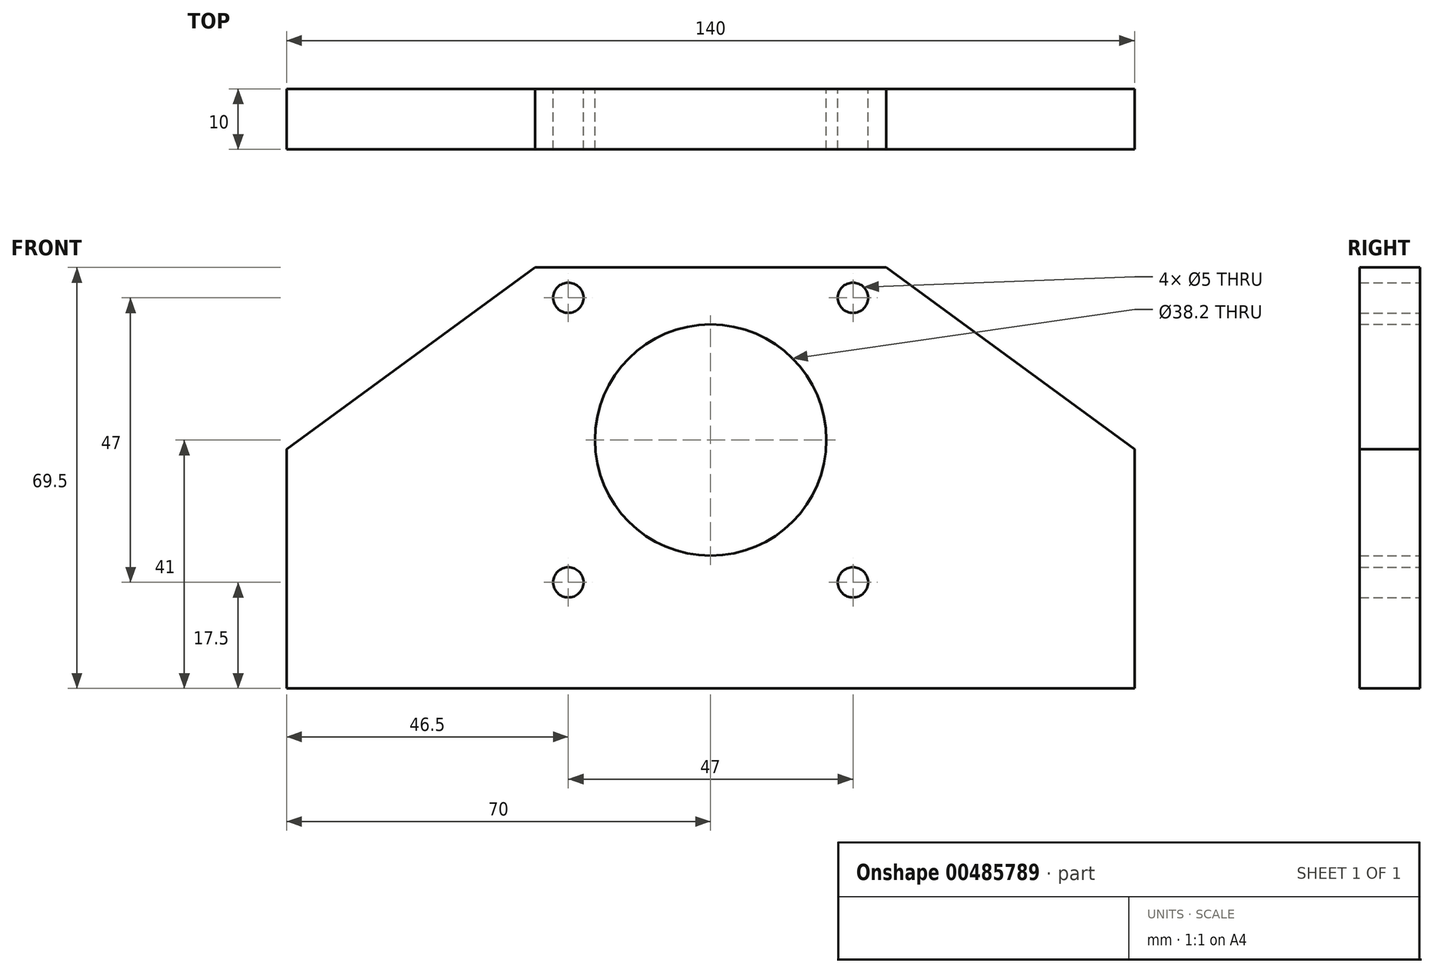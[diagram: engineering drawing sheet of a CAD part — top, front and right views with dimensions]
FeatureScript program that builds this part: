
annotation { "Feature Type Name" : "Feature", "Feature Type Description" : "" }
export const myFeature = defineFeature(function(context is Context, id is Id, definition is map)
    precondition{}
    {
        {
            var Q0;
            Q0=qCreatedBy(makeId("Front.planeOp"),FACE);
            var sketch = newSketch(context, id + "F0", { "sketchPlane" : qUnion([Q0])});
            skLineSegment(sketch, "E0.bottom", {"start": v(-23.5, 23.5) * mm, "end": v(23.5, 23.5) * mm, "construction": true});
            skLineSegment(sketch, "E0.top", {"start": v(-23.5, -23.5) * mm, "end": v(23.5, -23.5) * mm, "construction": true});
            skLineSegment(sketch, "E0.left", {"start": v(-23.5, 23.5) * mm, "end": v(-23.5, -23.5) * mm, "construction": true});
            skLineSegment(sketch, "E0.right", {"start": v(23.5, 23.5) * mm, "end": v(23.5, -23.5) * mm, "construction": true});
            skPoint(sketch, "E0.middle", {"position": v(0, 0) * mm});
            skLineSegment(sketch, "E1.bottom", {"start": v(-29, 28.5) * mm, "end": v(29, 28.5) * mm});
            skCircle(sketch, "E2", {"center": v(0, 0) * mm, "radius": 19.1 * mm});
            skLineSegment(sketch, "E3", {"start": v(-70, -41) * mm, "end": v(-70, -1.5) * mm});
            skLineSegment(sketch, "E4", {"start": v(-70, -1.5) * mm, "end": v(-29, 28.5) * mm});
            skLineSegment(sketch, "E5.MirrorCS", {"start": v(70, -1.5) * mm, "end": v(29, 28.5) * mm});
            skLineSegment(sketch, "E6.MirrorCS", {"start": v(70, -41) * mm, "end": v(70, -1.5) * mm});
            skCircle(sketch, "E7", {"center": v(-23.5, 23.5) * mm, "radius": 2.5 * mm});
            skCircle(sketch, "E8", {"center": v(-23.5, -23.5) * mm, "radius": 2.5 * mm});
            skCircle(sketch, "E9", {"center": v(23.5, -23.5) * mm, "radius": 2.5 * mm});
            skCircle(sketch, "E10", {"center": v(23.5, 23.5) * mm, "radius": 2.5 * mm});
            skLineSegment(sketch, "E11", {"start": v(-70, -41) * mm, "end": v(70, -41) * mm});
            skLineSegment(sketch, "E12", {"start": v(0, 0) * mm, "end": v(0, -41) * mm, "construction": true});
            skSolve(sketch);
        }
        {
            var Q0;
            Q0=qSketchRegion(id+"F0",true);
            extrude(context, id + "F1", {"entities" : qUnion([Q0]), "depth" : 10 * mm});
        }
    });
